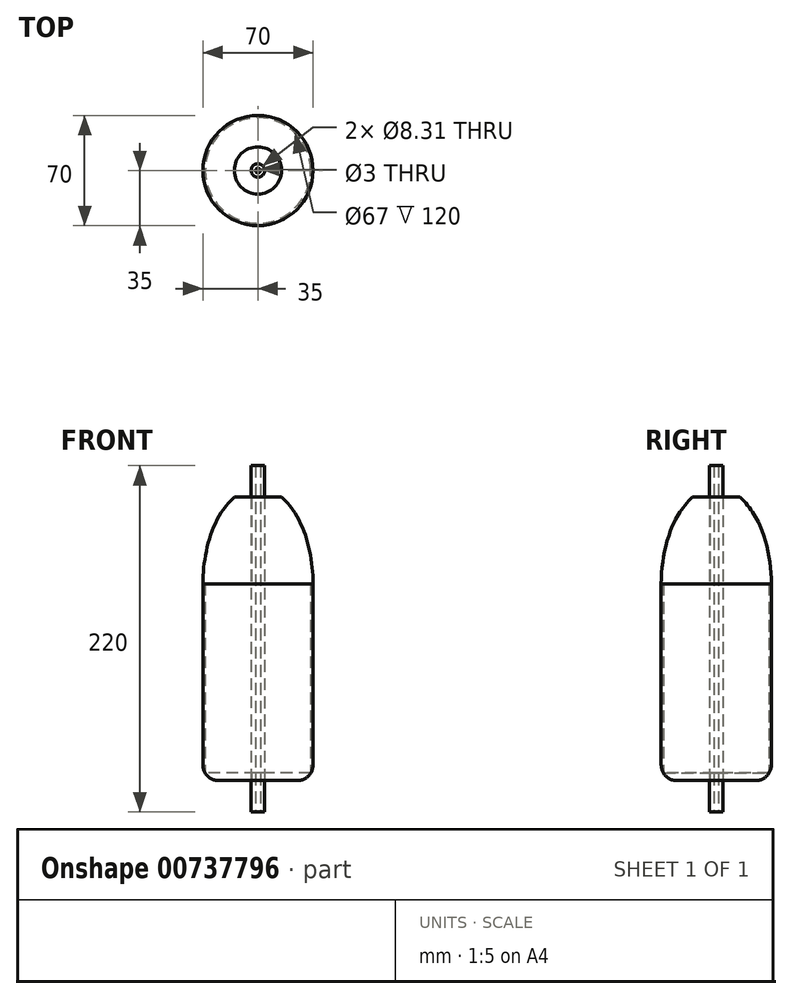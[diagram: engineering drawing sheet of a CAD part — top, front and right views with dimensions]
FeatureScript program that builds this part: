
annotation { "Feature Type Name" : "Feature", "Feature Type Description" : "" }
export const myFeature = defineFeature(function(context is Context, id is Id, definition is map)
    precondition{}
    {
        {
            var Q0;
            Q0=qCreatedBy(makeId("Top.planeOp"),FACE);
            var sketch = newSketch(context, id + "F0", { "sketchPlane" : qUnion([Q0])});
            skCircle(sketch, "E0", {"center": v(0, 0) * mm, "radius": 35 * mm});
            skCircle(sketch, "E1", {"center": v(0, 0) * mm, "radius": 33.5 * mm});
            skSolve(sketch);
        }
        {
            var Q0;
            Q0=makeQuery(id+"F0.imprint","IMPRINT",FACE,{"disambiguationData":[TD([[makeQuery(id+"F0.imprint","IMPRINT",EDGE,{"derivedFrom":sQuery(id+"F0.wireOp",EDGE,"E0")}),1.0]])]});
            extrude(context, id + "F1", {"entities" : qUnion([Q0]), "depth" : 125 * mm, "offsetDistance" : 25 * mm});
        }
        {
            var Q0;
            Q0=qCreatedBy(makeId("Top.planeOp"),FACE);
            var sketch = newSketch(context, id + "F2", { "sketchPlane" : qUnion([Q0])});
            skCircle(sketch, "E2", {"center": v(0, 0) * mm, "radius": 35 * mm});
            skSolve(sketch);
        }
        {
            var Q0;
            Q0 = qSketchRegion(id + "F2", true);
            extrude(context, id + "F3", {"entities" : qUnion([Q0]), "operationType" : NewBodyOperationType.ADD, "depth" : 5 * mm, "offsetDistance" : 25 * mm});
        }
        {
            var Q0;
            Q0=makeQuery(id+"F1.opExtrude","CAP_EDGE",EDGE,{"disambiguationData":[OSD([sQuery(id+"F0.wireOp",EDGE,"E0")])],"isStart":true});
            fillet(context, id + "F4", {"entities" : qUnion([Q0]), "radius" : 10 * mm, "tangentPropagation" : true, "allowEdgeOverflow" : false});
        }
        {
            var Q0;
            Q0=makeQuery(id+"F1.opExtrude","SWEPT_BODY",BODY,{"disambiguationData":[OSD([sQuery(id+"F0.wireOp",EDGE,"E0"),sQuery(id+"F0.wireOp",EDGE,"E1")])]});
            transform(context, id + "F5", {"entities" : qUnion([Q0]), "transformType" : TransformType.TRANSLATION_3D, "dx" : 0 * mm, "dy" : 0 * mm, "dz" : -125 * mm, "makeCopy" : false});
        }
        {
            var Q0;
            Q0=makeQuery(id+"F1.opExtrude","SWEPT_BODY",BODY,{"disambiguationData":[OSD([sQuery(id+"F0.wireOp",EDGE,"E0"),sQuery(id+"F0.wireOp",EDGE,"E1")])]});
            transform(context, id + "F6", {"entities" : qUnion([Q0]), "transformType" : TransformType.TRANSLATION_3D, "dx" : 0 * mm, "dy" : 0 * mm, "dz" : 145 * mm, "makeCopy" : false});
        }
        {
            var Q0;
            Q0=makeQuery(id+"F1.opExtrude","SWEPT_BODY",BODY,{"disambiguationData":[OSD([sQuery(id+"F0.wireOp",EDGE,"E0"),sQuery(id+"F0.wireOp",EDGE,"E1")])]});
            transform(context, id + "F7", {"entities" : qUnion([Q0]), "transformType" : TransformType.TRANSLATION_3D, "dx" : 0 * mm, "dy" : 0 * mm, "dz" : -145 * mm, "makeCopy" : false});
        }
        {
            var Q0;
            Q0=qCreatedBy(makeId("Front.planeOp"),FACE);
            var sketch = newSketch(context, id + "F8", { "sketchPlane" : qUnion([Q0])});
            skLineSegment(sketch, "E3", {"start": v(0, 0) * mm, "end": v(-35, 0) * mm});
            skLineSegment(sketch, "E4", {"start": v(0, 0) * mm, "end": v(0, 55) * mm});
            skLineSegment(sketch, "E5", {"start": v(0, 55) * mm, "end": v(-15, 55) * mm});
            skFitSpline(sketch, "E6", {"points": [v(-15, 55) * mm, v(-35, 0) * mm], "startDerivative": vector(-44.34, -39.62) * mm, "endDerivative": vector(-0.87, -57.87) * mm});
            skSolve(sketch);
        }
        {
            var Q0;
            Q0 = qSketchRegion(id + "F8", true);
            var Q1;
            Q1=sQuery(id+"F8.wireOp",EDGE,"E4");
            var Q2;
            Q2=sQuery(id+"F8.wireOp",EDGE,"E4");
            revolve(context, id + "F9", {"surfaceOperationType" : NewSurfaceOperationType.NEW, "entities" : qUnion([Q0]), "surfaceEntities" : qUnion([Q1]), "axis" : qUnion([Q2]), "revolveType" : RevolveType.FULL});
        }
        {
            var Q0;
            Q0=makeQuery(id+"F1.opExtrude","SWEPT_BODY",BODY,{"disambiguationData":[OSD([sQuery(id+"F0.wireOp",EDGE,"E0"),sQuery(id+"F0.wireOp",EDGE,"E1")])]});
            var Q1;
            Q1=makeQuery(id+"F9.opRevolve","SWEPT_BODY",BODY,{"disambiguationData":[OSD([sQuery(id+"F8.wireOp",EDGE,"E3"),sQuery(id+"F8.wireOp",EDGE,"E4"),sQuery(id+"F8.wireOp",EDGE,"E5"),sQuery(id+"F8.wireOp",EDGE,"E6")])]});
            transform(context, id + "F10", {"entities" : qUnion([Q0, Q1]), "transformType" : TransformType.TRANSLATION_3D, "dx" : 0 * mm, "dy" : 0 * mm, "dz" : 145 * mm, "makeCopy" : false});
        }
        {
            var Q0;
            Q0=qCreatedBy(makeId("Top.planeOp"),FACE);
            var sketch = newSketch(context, id + "F11", { "sketchPlane" : qUnion([Q0])});
            skCircle(sketch, "E7", {"center": v(0, 0) * mm, "radius": 4.15 * mm});
            skSolve(sketch);
        }
        {
            var Q0;
            Q0=makeQuery(id+"F11.imprint","IMPRINT",FACE,{"disambiguationData":[TD([[makeQuery(id+"F11.imprint","IMPRINT",EDGE,{"derivedFrom":sQuery(id+"F11.wireOp",EDGE,"E7")}),1.0]])]});
            var Q1;
            Q1=sQuery(id+"F11.wireOp",EDGE,"E7");
            extrude(context, id + "F12", {"entities" : qUnion([Q0]), "operationType" : NewBodyOperationType.REMOVE, "surfaceEntities" : qUnion([Q1]), "oppositeDirection" : true, "depth" : -210 * mm, "offsetDistance" : 25 * mm});
        }
        {
            var Q0;
            Q0=qCreatedBy(makeId("Top.planeOp"),FACE);
            var sketch = newSketch(context, id + "F13", { "sketchPlane" : qUnion([Q0])});
            skCircle(sketch, "E8", {"center": v(0, 0) * mm, "radius": 4.3 * mm});
            skCircle(sketch, "E9", {"center": v(0, 0) * mm, "radius": 1.5 * mm});
            skSolve(sketch);
        }
        {
            var Q0;
            Q0=makeQuery(id+"F13.imprint","IMPRINT",FACE,{"disambiguationData":[TD([[makeQuery(id+"F13.imprint","IMPRINT",EDGE,{"derivedFrom":sQuery(id+"F13.wireOp",EDGE,"E8")}),1.0]])]});
            var Q1;
            Q1=sQuery(id+"F13.wireOp",EDGE,"E8");
            extrude(context, id + "F14", {"entities" : qUnion([Q0]), "surfaceEntities" : qUnion([Q1]), "depth" : 220 * mm, "offsetDistance" : 25 * mm});
        }
        {
            var Q0;
            Q0=makeQuery(id+"F1.opExtrude","SWEPT_BODY",BODY,{"disambiguationData":[OSD([sQuery(id+"F0.wireOp",EDGE,"E0"),sQuery(id+"F0.wireOp",EDGE,"E1")])]});
            var Q1;
            Q1=makeQuery(id+"F9.opRevolve","SWEPT_BODY",BODY,{"disambiguationData":[OSD([sQuery(id+"F8.wireOp",EDGE,"E3"),sQuery(id+"F8.wireOp",EDGE,"E4"),sQuery(id+"F8.wireOp",EDGE,"E5"),sQuery(id+"F8.wireOp",EDGE,"E6")])]});
            var Q2;
            Q2=makeQuery(id+"F14.opExtrude","SWEPT_BODY",BODY,{"disambiguationData":[OSD([sQuery(id+"F13.wireOp",EDGE,"E8"),sQuery(id+"F13.wireOp",EDGE,"E9")])]});
            transform(context, id + "F15", {"entities" : qUnion([Q0, Q1, Q2]), "transformType" : TransformType.TRANSLATION_3D, "dx" : 0 * mm, "dy" : 35 * mm, "dz" : -85 * mm, "makeCopy" : false});
        }
        {
            var Q0;
            Q0=makeQuery(id+"F1.opExtrude","SWEPT_BODY",BODY,{"disambiguationData":[OSD([sQuery(id+"F0.wireOp",EDGE,"E0"),sQuery(id+"F0.wireOp",EDGE,"E1")])]});
            var Q1;
            Q1=makeQuery(id+"F9.opRevolve","SWEPT_BODY",BODY,{"disambiguationData":[OSD([sQuery(id+"F8.wireOp",EDGE,"E3"),sQuery(id+"F8.wireOp",EDGE,"E4"),sQuery(id+"F8.wireOp",EDGE,"E5"),sQuery(id+"F8.wireOp",EDGE,"E6")])]});
            var Q2;
            Q2=makeQuery(id+"F14.opExtrude","SWEPT_BODY",BODY,{"disambiguationData":[OSD([sQuery(id+"F13.wireOp",EDGE,"E8"),sQuery(id+"F13.wireOp",EDGE,"E9")])]});
            transform(context, id + "F16", {"entities" : qUnion([Q0, Q1, Q2]), "transformType" : TransformType.TRANSLATION_3D, "dx" : 0 * mm, "dy" : -35 * mm, "dz" : 85 * mm, "makeCopy" : false});
        }
    });
